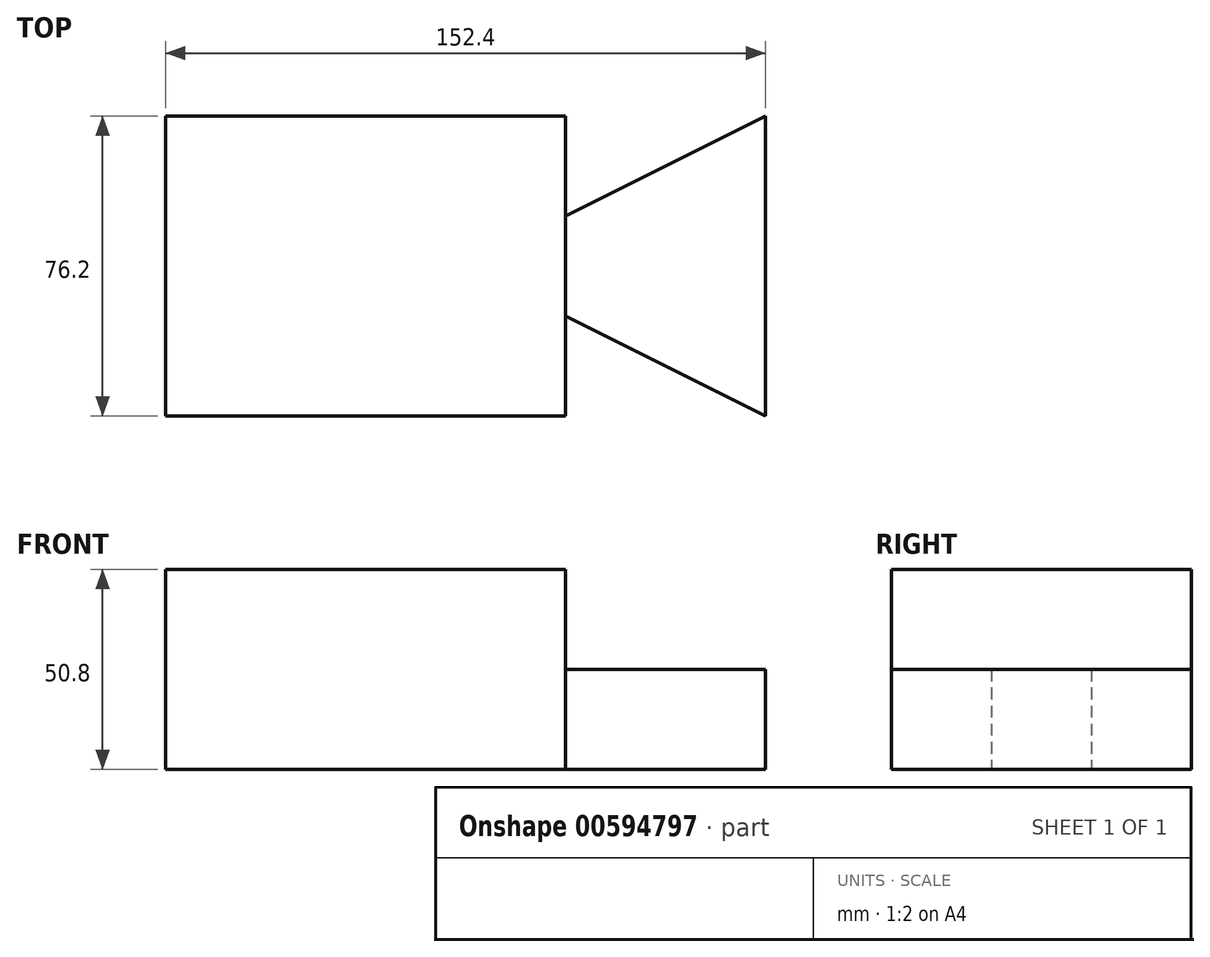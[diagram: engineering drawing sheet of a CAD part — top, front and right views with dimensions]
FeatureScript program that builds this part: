
annotation { "Feature Type Name" : "Feature", "Feature Type Description" : "" }
export const myFeature = defineFeature(function(context is Context, id is Id, definition is map)
    precondition{}
    {
        {
            var Q0;
            Q0=qCreatedBy(makeId("Top.planeOp"),FACE);
            var sketch = newSketch(context, id + "F0", { "sketchPlane" : qUnion([Q0])});
            skLineSegment(sketch, "E0", {"start": v(-71.76, 41.95) * mm, "end": v(-71.76, -34.25) * mm});
            skLineSegment(sketch, "E1", {"start": v(-71.76, -34.25) * mm, "end": v(29.84, -34.25) * mm});
            skLineSegment(sketch, "E2", {"start": v(29.84, -34.25) * mm, "end": v(29.84, 41.95) * mm});
            skLineSegment(sketch, "E3", {"start": v(29.84, 41.95) * mm, "end": v(-71.76, 41.95) * mm});
            skLineSegment(sketch, "E4", {"start": v(29.84, 41.95) * mm, "end": v(29.84, 16.55) * mm});
            skLineSegment(sketch, "E5", {"start": v(29.84, -8.85) * mm, "end": v(29.84, -34.25) * mm});
            skLineSegment(sketch, "E6", {"start": v(29.84, 16.55) * mm, "end": v(80.64, 41.95) * mm});
            skLineSegment(sketch, "E7", {"start": v(29.84, -8.85) * mm, "end": v(80.64, -34.25) * mm});
            skLineSegment(sketch, "E8", {"start": v(80.64, 41.95) * mm, "end": v(80.64, -34.25) * mm});
            skSolve(sketch);
        }
        {
            var Q0;
            Q0=makeQuery(id+"F0.imprint","IMPRINT",FACE,{"disambiguationData":[TD([[makeQuery(id+"F0.imprint","IMPRINT",EDGE,{"derivedFrom":sQuery(id+"F0.wireOp",EDGE,"E2")}),-1.0]])]});
            extrude(context, id + "F1", {"entities" : qUnion([Q0]), "depth" : 25.4 * mm, "offsetDistance" : 25.4 * mm});
        }
        {
            var Q0;
            Q0=makeQuery(id+"F0.imprint","IMPRINT",FACE,{"disambiguationData":[TD([[makeQuery(id+"F0.imprint","IMPRINT",EDGE,{"derivedFrom":sQuery(id+"F0.wireOp",EDGE,"E0")}),1.0]])]});
            extrude(context, id + "F2", {"entities" : qUnion([Q0]), "operationType" : NewBodyOperationType.ADD, "depth" : 50.8 * mm, "offsetDistance" : 25.4 * mm});
        }
    });
